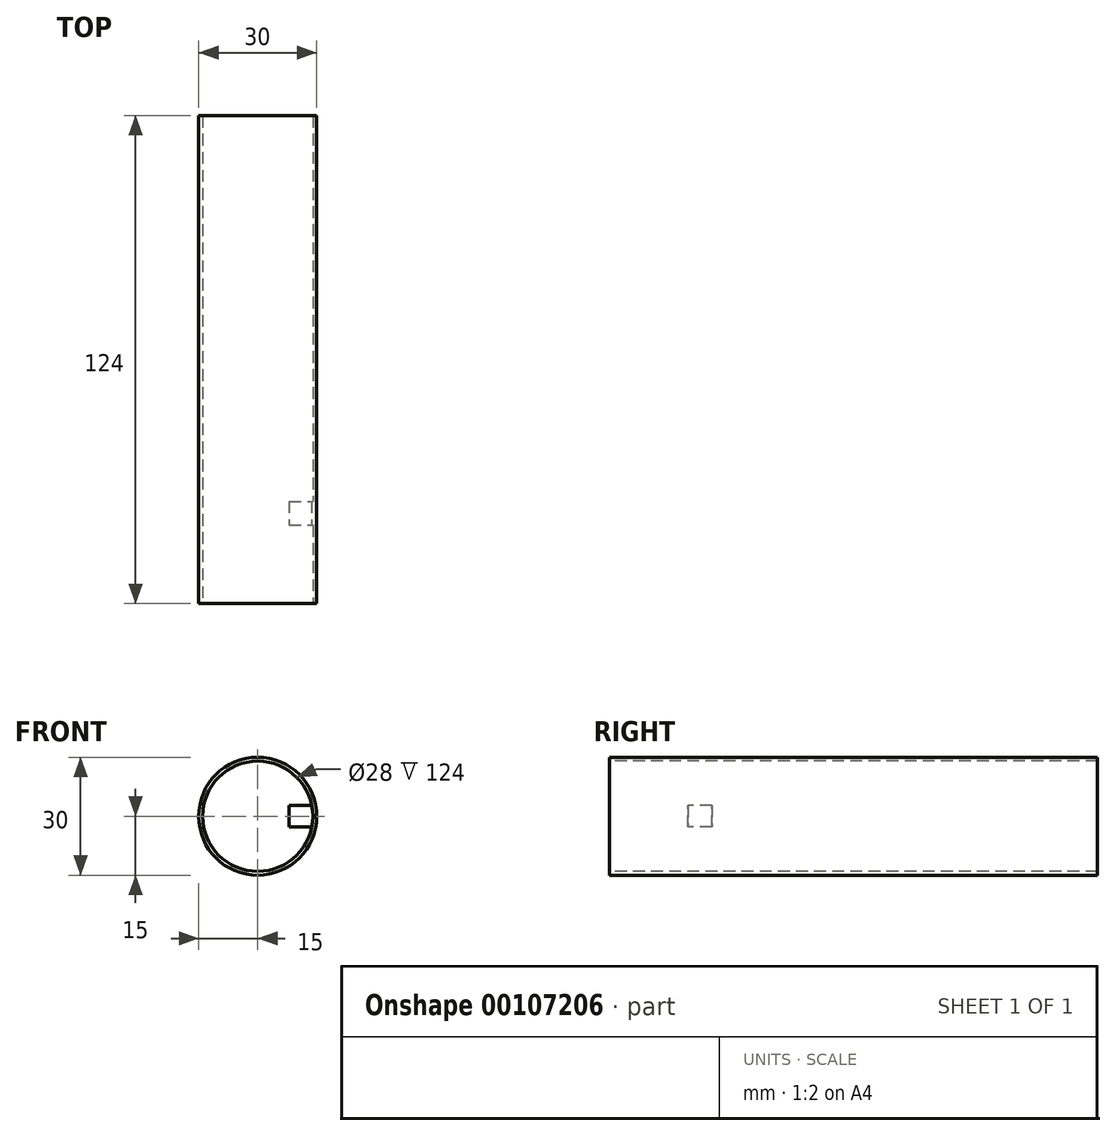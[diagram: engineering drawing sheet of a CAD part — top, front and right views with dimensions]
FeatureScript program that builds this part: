
annotation { "Feature Type Name" : "Feature", "Feature Type Description" : "" }
export const myFeature = defineFeature(function(context is Context, id is Id, definition is map)
    precondition{}
    {
        {
            var Q0;
            Q0=qCreatedBy(makeId("Front.planeOp"),FACE);
            var sketch = newSketch(context, id + "F0", { "sketchPlane" : qUnion([Q0])});
            skCircle(sketch, "E0", {"center": v(0, 0) * mm, "radius": 15 * mm});
            skCircle(sketch, "E1", {"center": v(0, 0) * mm, "radius": 14 * mm});
            skSolve(sketch);
        }
        {
            var Q0;
            Q0=makeQuery(id+"F0.imprint","IMPRINT",FACE,{"disambiguationData":[TD([[makeQuery(id+"F0.imprint","IMPRINT",EDGE,{"derivedFrom":sQuery(id+"F0.wireOp",EDGE,"E0")}),1.0]])]});
            extrude(context, id + "F1", {"entities" : qUnion([Q0]), "oppositeDirection" : true, "depth" : 124 * mm});
        }
        {
            var Q0;
            Q0=qCreatedBy(makeId("Front.planeOp"),FACE);
            cPlane(context, id + "F2", {"entities" : qUnion([Q0]), "cplaneType" : CPlaneType.OFFSET, "offset" : 20 * mm, "oppositeDirection" : true, "width" : 150 * mm, "height" : 150 * mm});
        }
        {
            var Q0;
            Q0=qCreatedBy(id+"F2.planeOp",FACE);
            var sketch = newSketch(context, id + "F3", { "sketchPlane" : qUnion([Q0])});
            skLineSegment(sketch, "E2.bottom", {"start": v(8, 2.75) * mm, "end": v(14.18, 2.75) * mm});
            skLineSegment(sketch, "E2.top", {"start": v(8, -2.75) * mm, "end": v(14.18, -2.75) * mm});
            skLineSegment(sketch, "E2.left", {"start": v(8, 2.75) * mm, "end": v(8, -2.75) * mm});
            skLineSegment(sketch, "E2.right", {"start": v(14.18, 2.75) * mm, "end": v(14.18, -2.75) * mm});
            skPoint(sketch, "E3", {"position": v(8, 0) * mm});
            skSolve(sketch);
        }
        {
            var Q0;
            Q0=makeQuery(id+"F3.imprint","IMPRINT",FACE,{"disambiguationData":[TD([[makeQuery(id+"F3.imprint","IMPRINT",EDGE,{"derivedFrom":sQuery(id+"F3.wireOp",EDGE,"E2.bottom")}),-1.0]])]});
            extrude(context, id + "F4", {"entities" : qUnion([Q0]), "operationType" : NewBodyOperationType.ADD, "oppositeDirection" : true, "depth" : 6 * mm});
        }
    });
